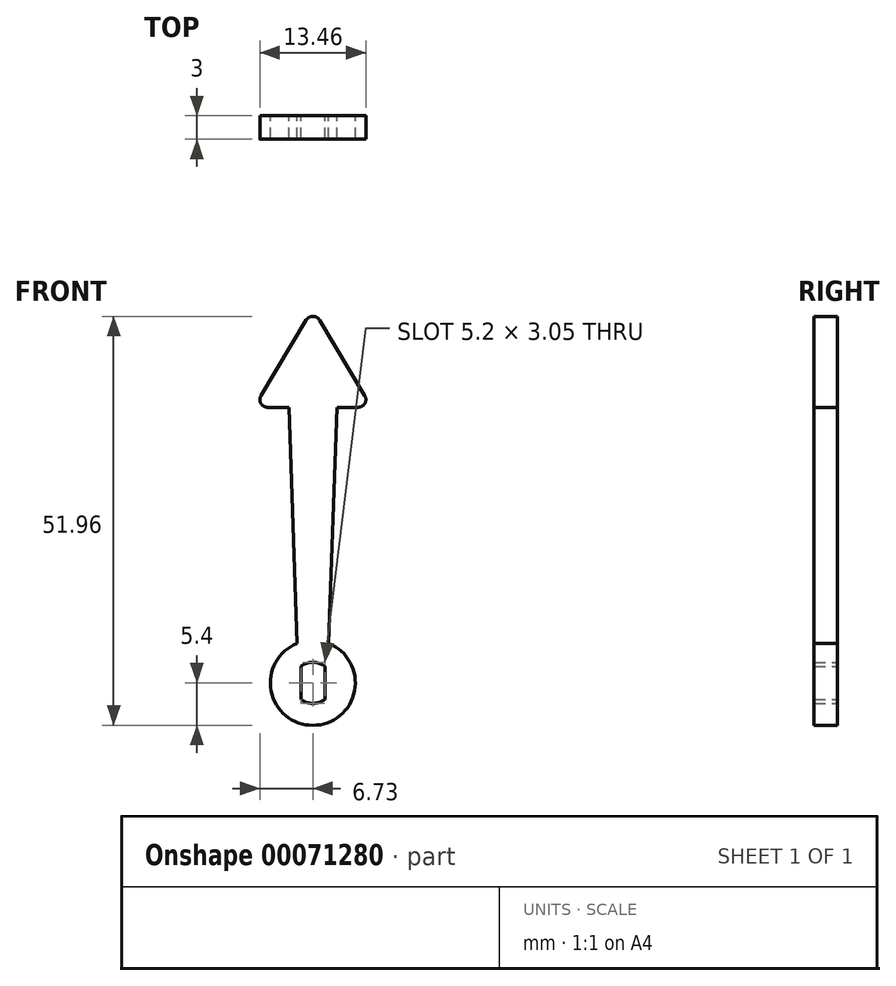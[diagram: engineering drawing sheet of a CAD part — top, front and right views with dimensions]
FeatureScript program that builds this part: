
annotation { "Feature Type Name" : "Feature", "Feature Type Description" : "" }
export const myFeature = defineFeature(function(context is Context, id is Id, definition is map)
    precondition{}
    {
        {
            var Q0;
            Q0=qCreatedBy(makeId("Front.planeOp"),FACE);
            var sketch = newSketch(context, id + "F0", { "sketchPlane" : qUnion([Q0])});
            skCircle(sketch, "E0", {"center": v(0, 0) * mm, "radius": 5.4 * mm});
            skCircle(sketch, "E1", {"center": v(0, 0) * mm, "radius": 2.6 * mm});
            skLineSegment(sketch, "E2", {"start": v(-1.52, 2.1) * mm, "end": v(-1.52, -2.1) * mm});
            skLineSegment(sketch, "E3", {"start": v(1.53, 2.1) * mm, "end": v(1.53, -2.1) * mm});
            skSolve(sketch);
        }
        {
            var Q0;
            Q0=makeQuery(id+"F0.imprint","IMPRINT",FACE,{"disambiguationData":[TD([[makeQuery(id+"F0.imprint","IMPRINT",EDGE,{"derivedFrom":sQuery(id+"F0.wireOp",EDGE,"E0")}),1.0]])]});
            var Q1;
            {var subQ0=sQuery(id+"F0.wireOp",EDGE,"E2");Q1=makeQuery(id+"F0.imprint","IMPRINT",FACE,{"disambiguationData":[TD([[makeQuery(id+"F0.imprint","IMPRINT",EDGE,{"derivedFrom":subQ0}),-1.0]])]});}
            var Q2;
            {var subQ0=sQuery(id+"F0.wireOp",EDGE,"E3");Q2=makeQuery(id+"F0.imprint","IMPRINT",FACE,{"disambiguationData":[TD([[makeQuery(id+"F0.imprint","IMPRINT",EDGE,{"derivedFrom":subQ0}),1.0]])]});}
            extrude(context, id + "F1", {"entities" : qUnion([Q0, Q1, Q2]), "depth" : 3 * mm});
        }
        {
            var Q0;
            Q0=qCreatedBy(makeId("Front.planeOp"),FACE);
            var sketch = newSketch(context, id + "F2", { "sketchPlane" : qUnion([Q0])});
            skLineSegment(sketch, "E4", {"start": v(0, 0) * mm, "end": v(0, 35) * mm, "construction": true});
            skLineSegment(sketch, "E5", {"start": v(0, 35) * mm, "end": v(3.05, 35) * mm});
            skLineSegment(sketch, "E6", {"start": v(0, 5.02) * mm, "end": v(2, 5.02) * mm});
            skLineSegment(sketch, "E7", {"start": v(2, 5.02) * mm, "end": v(3.05, 35) * mm});
            skLineSegment(sketch, "E8.MirrorCS", {"start": v(0, 5.02) * mm, "end": v(-2, 5.02) * mm});
            skLineSegment(sketch, "E9.MirrorCS", {"start": v(0, 35) * mm, "end": v(-3.05, 35) * mm});
            skLineSegment(sketch, "E10.MirrorCS", {"start": v(-2, 5.02) * mm, "end": v(-3.05, 35) * mm});
            skSolve(sketch);
        }
        {
            var Q0;
            Q0=makeQuery(id+"F2.imprint","IMPRINT",FACE,{"disambiguationData":[TD([[makeQuery(id+"F2.imprint","IMPRINT",EDGE,{"derivedFrom":sQuery(id+"F2.wireOp",EDGE,"E5")}),-1.0]])]});
            var Q1;
            Q1=makeQuery(id+"F1.opExtrude","CAP_FACE",FACE,{"disambiguationData":[OSD([sQuery(id+"F0.wireOp",EDGE,"E0"),sQuery(id+"F0.wireOp",EDGE,"E1"),sQuery(id+"F0.wireOp",EDGE,"E2"),sQuery(id+"F0.wireOp",EDGE,"E3")])],"isStart":false});
            extrude(context, id + "F3", {"entities" : qUnion([Q0]), "operationType" : NewBodyOperationType.ADD, "endBound" : BoundingType.UP_TO_SURFACE, "endBoundEntityFace" : qUnion([Q1]), "depth" : 25 * mm});
        }
        {
            var Q0;
            Q0=qCreatedBy(makeId("Front.planeOp"),FACE);
            var sketch = newSketch(context, id + "F4", { "sketchPlane" : qUnion([Q0])});
            skLineSegment(sketch, "E11", {"start": v(0, 35) * mm, "end": v(0, 47.5) * mm, "construction": true});
            skLineSegment(sketch, "E12", {"start": v(-7.5, 35) * mm, "end": v(7.5, 35) * mm});
            skLineSegment(sketch, "E13", {"start": v(-7.5, 35) * mm, "end": v(0, 47.5) * mm});
            skLineSegment(sketch, "E14", {"start": v(7.5, 35) * mm, "end": v(0, 47.5) * mm});
            skSolve(sketch);
        }
        {
            var Q0;
            Q0=makeQuery(id+"F4.imprint","IMPRINT",FACE,{"disambiguationData":[TD([[makeQuery(id+"F4.imprint","IMPRINT",EDGE,{"derivedFrom":sQuery(id+"F4.wireOp",EDGE,"E12")}),1.0]])]});
            var Q1;
            Q1=makeQuery(id+"F3.boolean.opBoolean","MERGE",FACE,{"derivedFrom":[makeQuery(id+"F1.opExtrude","CAP_FACE",FACE,{"disambiguationData":[OSD([sQuery(id+"F0.wireOp",EDGE,"E0"),sQuery(id+"F0.wireOp",EDGE,"E1"),sQuery(id+"F0.wireOp",EDGE,"E2"),sQuery(id+"F0.wireOp",EDGE,"E3")])],"isStart":false}),makeQuery(id+"F3.opExtrude","CAP_FACE",FACE,{"disambiguationData":[OSD([sQuery(id+"F2.wireOp",EDGE,"E5"),sQuery(id+"F2.wireOp",EDGE,"E6"),sQuery(id+"F2.wireOp",EDGE,"E7"),sQuery(id+"F2.wireOp",EDGE,"E8.MirrorCS"),sQuery(id+"F2.wireOp",EDGE,"E9.MirrorCS"),sQuery(id+"F2.wireOp",EDGE,"E10.MirrorCS")])],"isStart":false})]});
            extrude(context, id + "F5", {"entities" : qUnion([Q0]), "operationType" : NewBodyOperationType.ADD, "endBound" : BoundingType.UP_TO_SURFACE, "endBoundEntityFace" : qUnion([Q1]), "depth" : 25 * mm});
        }
        {
            var Q0;
            Q0=makeQuery(id+"F5.opExtrude","SWEPT_EDGE",EDGE,{"disambiguationData":[OSD([sQuery(id+"F4.wireOp",EDGE,"E12"),sQuery(id+"F4.wireOp",EDGE,"E13")])]});
            var Q1;
            Q1=makeQuery(id+"F5.opExtrude","SWEPT_EDGE",EDGE,{"disambiguationData":[OSD([sQuery(id+"F4.wireOp",EDGE,"E13"),sQuery(id+"F4.wireOp",EDGE,"E14")])]});
            var Q2;
            Q2=makeQuery(id+"F5.opExtrude","SWEPT_EDGE",EDGE,{"disambiguationData":[OSD([sQuery(id+"F4.wireOp",EDGE,"E12"),sQuery(id+"F4.wireOp",EDGE,"E14")])]});
            fillet(context, id + "F6", {"entities" : qUnion([Q0, Q1, Q2]), "radius" : 1 * mm, "tangentPropagation" : true, "allowEdgeOverflow" : false});
        }
    });
